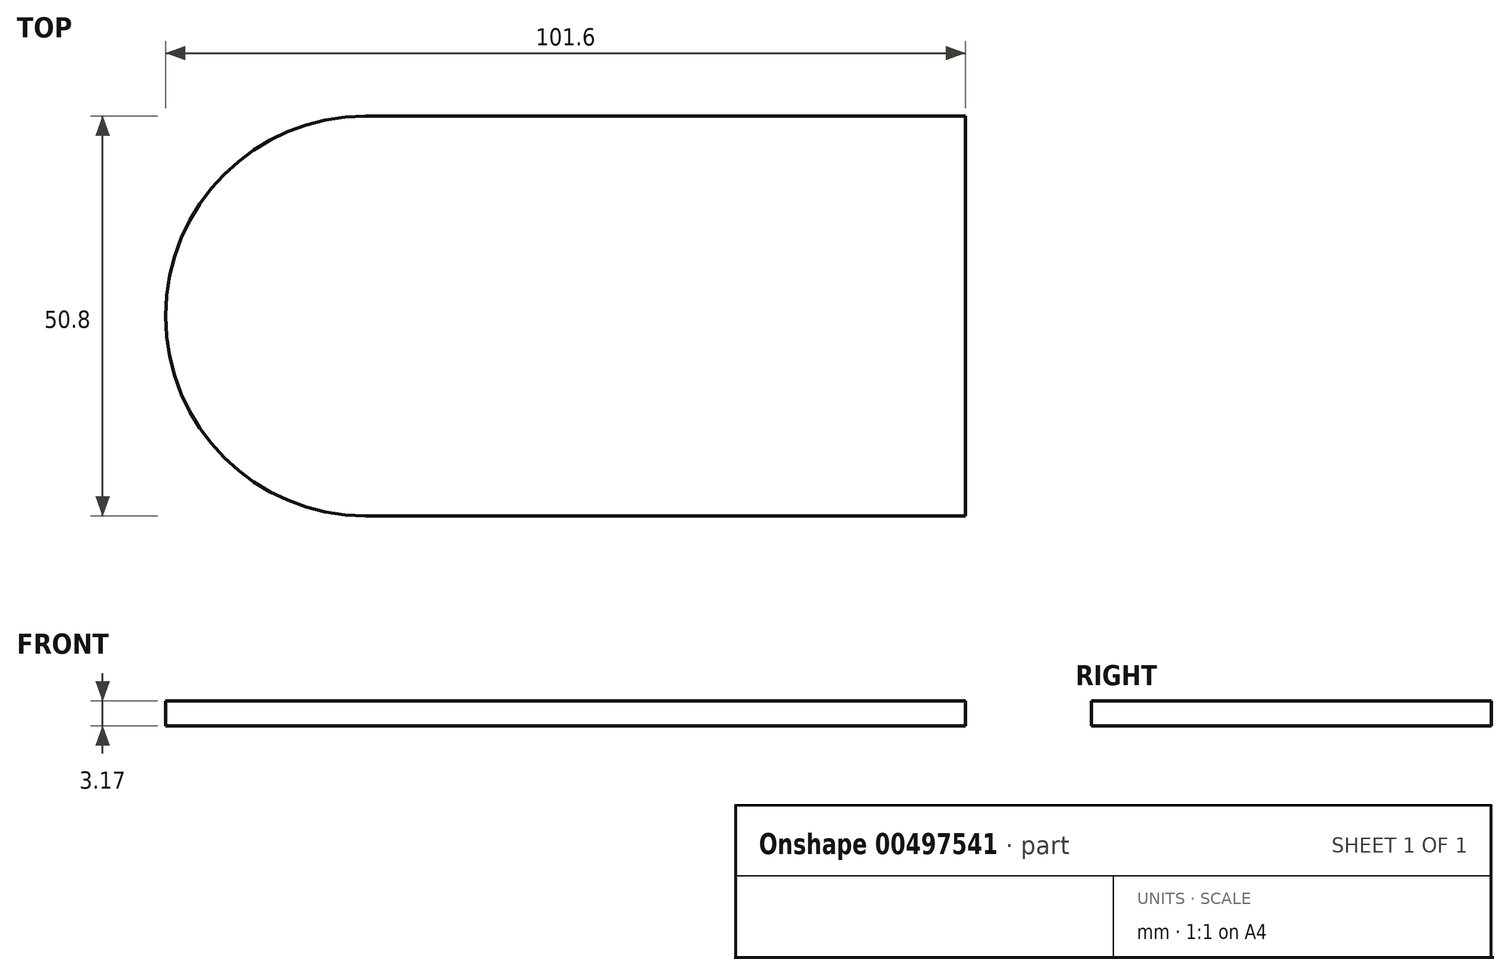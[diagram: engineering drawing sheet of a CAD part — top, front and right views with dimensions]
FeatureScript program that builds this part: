
annotation { "Feature Type Name" : "Feature", "Feature Type Description" : "" }
export const myFeature = defineFeature(function(context is Context, id is Id, definition is map)
    precondition{}
    {
        {
            var Q0;
            Q0=qCreatedBy(makeId("Top.planeOp"),FACE);
            var sketch = newSketch(context, id + "F0", { "sketchPlane" : qUnion([Q0])});
            skLineSegment(sketch, "E0.bottom", {"start": v(0, 0) * mm, "end": v(76.2, 0) * mm});
            skLineSegment(sketch, "E0.top", {"start": v(0, 50.8) * mm, "end": v(76.2, 50.8) * mm});
            skLineSegment(sketch, "E0.left", {"start": v(0, 0) * mm, "end": v(0, 50.8) * mm});
            skLineSegment(sketch, "E0.right", {"start": v(76.2, 0) * mm, "end": v(76.2, 50.8) * mm});
            skArc(sketch, "E1", {"start": v(0, 50.8) * mm, "mid": v(-25.4, 25.4) * mm, "end": v(0, 0) * mm});
            skSolve(sketch);
        }
        {
            var Q0;
            Q0=makeQuery(id+"F0.imprint","IMPRINT",FACE,{"disambiguationData":[TD([[makeQuery(id+"F0.imprint","IMPRINT",EDGE,{"derivedFrom":sQuery(id+"F0.wireOp",EDGE,"E0.bottom")}),1.0]])]});
            var Q1;
            Q1=makeQuery(id+"F0.imprint","IMPRINT",FACE,{"disambiguationData":[TD([[makeQuery(id+"F0.imprint","IMPRINT",EDGE,{"derivedFrom":sQuery(id+"F0.wireOp",EDGE,"E0.left")}),1.0]])]});
            extrude(context, id + "F1", {"entities" : qUnion([Q0, Q1]), "depth" : 3.17 * mm});
        }
    });
